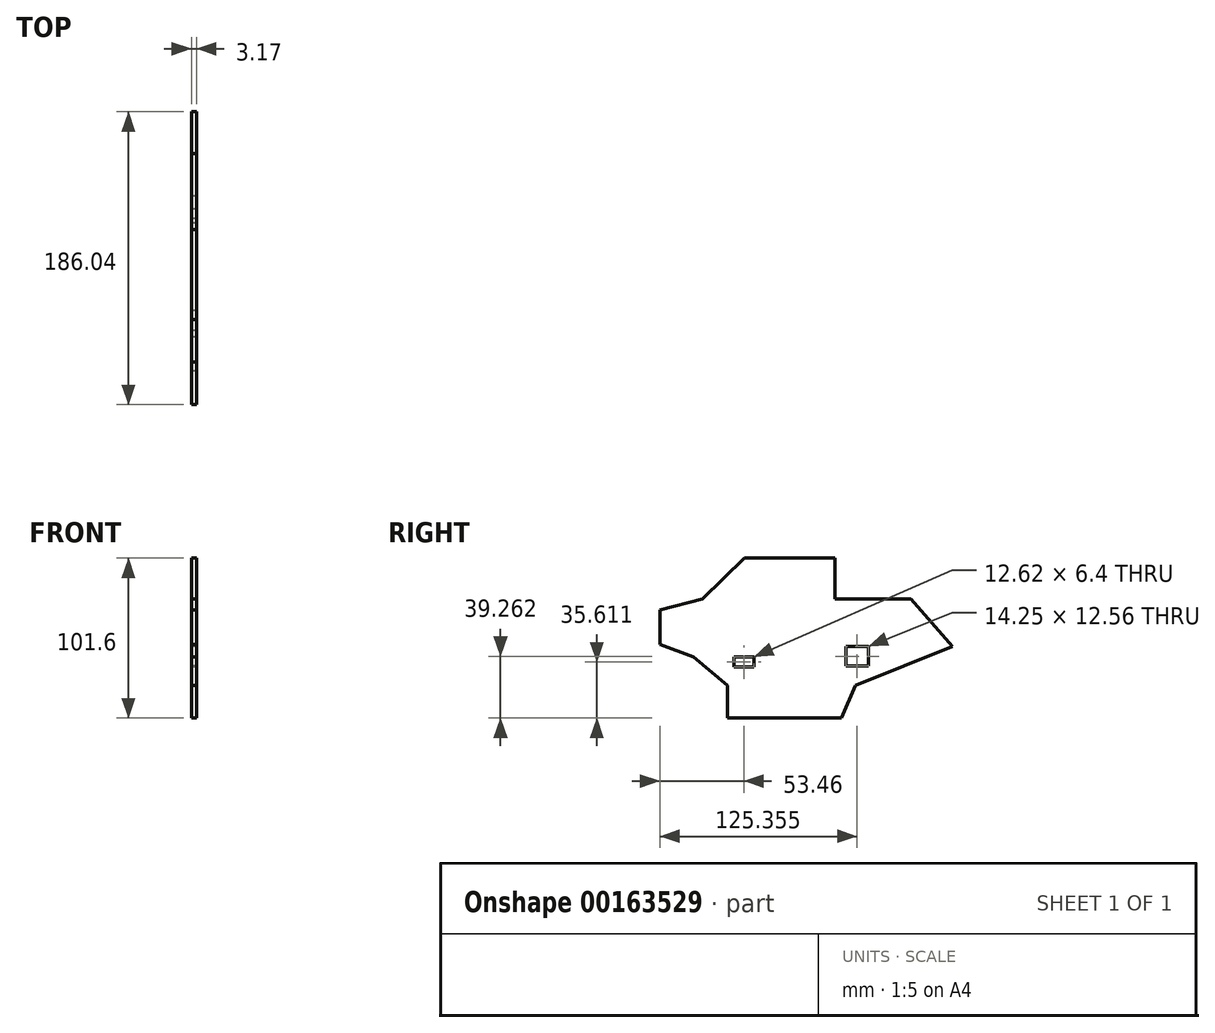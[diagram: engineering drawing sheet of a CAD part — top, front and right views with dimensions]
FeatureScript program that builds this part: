
annotation { "Feature Type Name" : "Feature", "Feature Type Description" : "" }
export const myFeature = defineFeature(function(context is Context, id is Id, definition is map)
    precondition{}
    {
        {
            var Q0;
            Q0=qCreatedBy(makeId("Right.planeOp"),FACE);
            var sketch = newSketch(context, id + "F1", { "sketchPlane" : qUnion([Q0])});
            skLineSegment(sketch, "E0", {"start": v(-54.78, 30.1) * mm, "end": v(-27.87, 56.06) * mm});
            skLineSegment(sketch, "E1", {"start": v(-27.87, 56.06) * mm, "end": v(29.36, 56.06) * mm});
            skLineSegment(sketch, "E2", {"start": v(29.36, 56.06) * mm, "end": v(29.36, 30.15) * mm});
            skLineSegment(sketch, "E3", {"start": v(29.36, 30.15) * mm, "end": v(77.69, 30.15) * mm});
            skLineSegment(sketch, "E4.bottom", {"start": v(-34.65, -6.73) * mm, "end": v(-22.03, -6.73) * mm});
            skLineSegment(sketch, "E4.top", {"start": v(-34.65, -13.13) * mm, "end": v(-22.03, -13.13) * mm});
            skLineSegment(sketch, "E4.left", {"start": v(-34.65, -6.73) * mm, "end": v(-34.65, -13.13) * mm});
            skLineSegment(sketch, "E4.right", {"start": v(-22.03, -6.73) * mm, "end": v(-22.03, -13.13) * mm});
            skLineSegment(sketch, "E5.bottom", {"start": v(36.43, 0) * mm, "end": v(50.68, 0) * mm});
            skLineSegment(sketch, "E5.top", {"start": v(36.43, -12.56) * mm, "end": v(50.68, -12.56) * mm});
            skLineSegment(sketch, "E5.left", {"start": v(36.43, 0) * mm, "end": v(36.43, -12.56) * mm});
            skLineSegment(sketch, "E5.right", {"start": v(50.68, 0) * mm, "end": v(50.68, -12.56) * mm});
            skLineSegment(sketch, "E6", {"start": v(0.75, 56.06) * mm, "end": v(0.75, -45.54) * mm});
            skLineSegment(sketch, "E7", {"start": v(-54.78, 30.1) * mm, "end": v(-81.8, 23.1) * mm});
            skLineSegment(sketch, "E8", {"start": v(-81.8, 23.1) * mm, "end": v(-81.8, 1.16) * mm});
            skLineSegment(sketch, "E9", {"start": v(-81.8, 1.16) * mm, "end": v(-60.42, -6.73) * mm});
            skLineSegment(sketch, "E10", {"start": v(-60.42, -6.73) * mm, "end": v(-38.76, -24.87) * mm});
            skLineSegment(sketch, "E11", {"start": v(-38.76, -24.87) * mm, "end": v(-38.76, -45.54) * mm});
            skLineSegment(sketch, "E12", {"start": v(-38.76, -45.54) * mm, "end": v(12.29, -45.54) * mm});
            skLineSegment(sketch, "E13", {"start": v(77.69, 30.15) * mm, "end": v(104.24, 0) * mm});
            skLineSegment(sketch, "E14", {"start": v(104.24, 0) * mm, "end": v(42.52, -24.87) * mm});
            skLineSegment(sketch, "E15", {"start": v(42.52, -24.87) * mm, "end": v(33.5, -45.54) * mm});
            skLineSegment(sketch, "E16", {"start": v(33.5, -45.54) * mm, "end": v(12.29, -45.54) * mm});
            skSolve(sketch);
        }
        {
            var Q0;
            Q0 = qSketchRegion(id + "F1", true);
            extrude(context, id + "F0", {"entities" : qUnion([Q0]), "depth" : 3.17 * mm});
        }
    });
